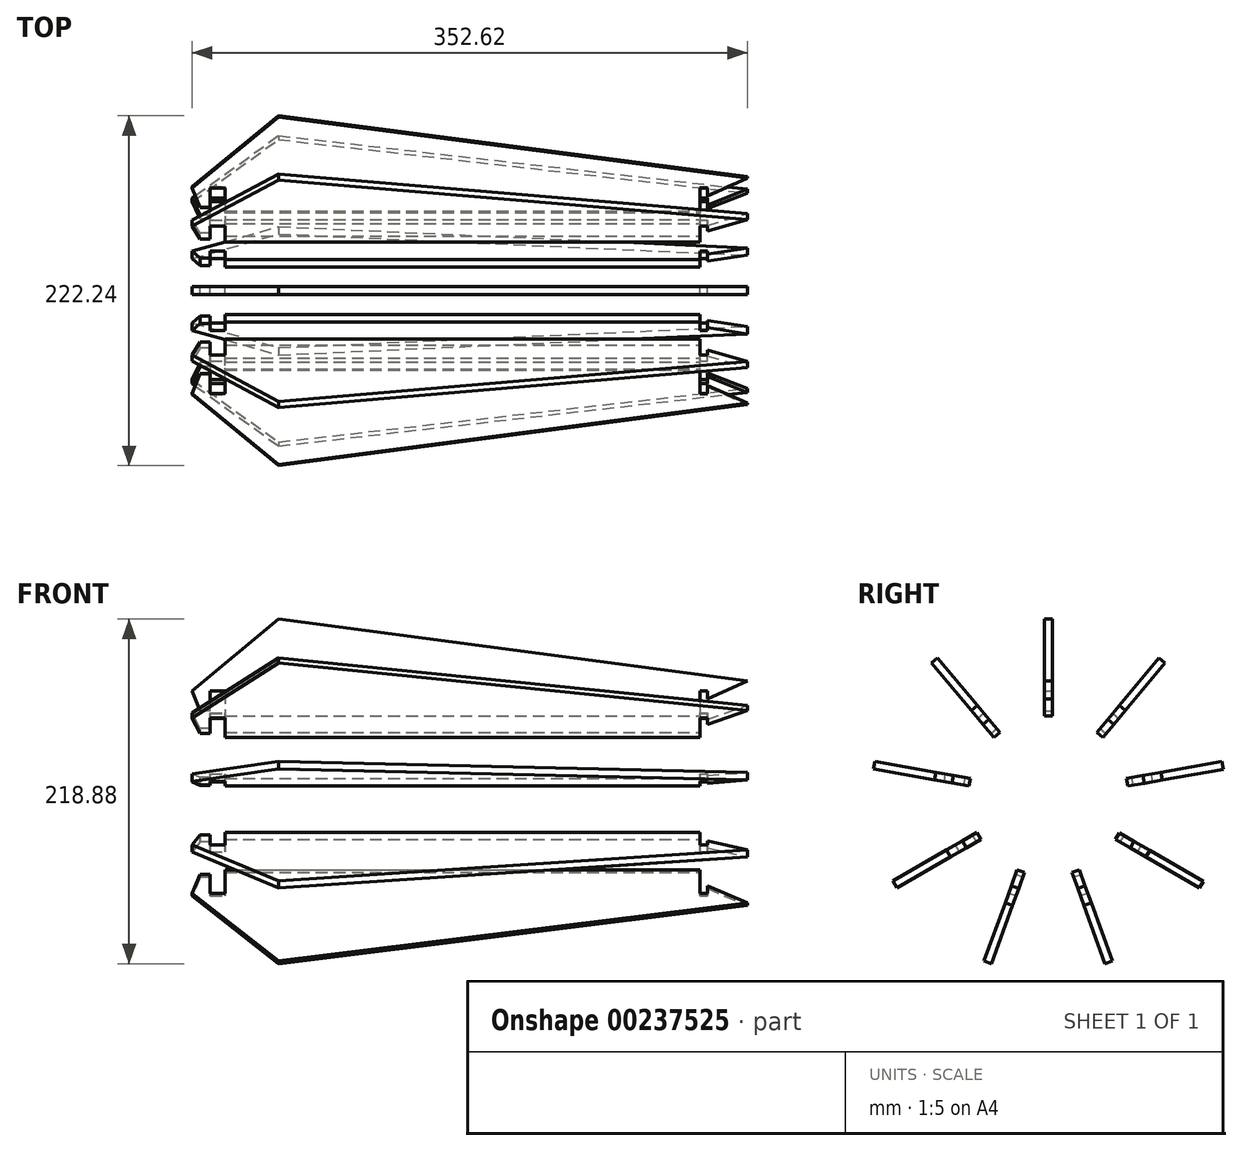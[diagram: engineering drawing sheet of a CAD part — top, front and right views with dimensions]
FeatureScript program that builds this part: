
annotation { "Feature Type Name" : "Feature", "Feature Type Description" : "" }
export const myFeature = defineFeature(function(context is Context, id is Id, definition is map)
    precondition{}
    {
        {
            var Q0;
            Q0=qCreatedBy(makeId("Front.planeOp"),FACE);
            var sketch = newSketch(context, id + "F0", { "sketchPlane" : qUnion([Q0])});
            skLineSegment(sketch, "E0", {"start": v(0, 0) * mm, "end": v(0, 12.7) * mm});
            skLineSegment(sketch, "E1", {"start": v(0, 12.7) * mm, "end": v(9.46, 12.7) * mm});
            skLineSegment(sketch, "E2", {"start": v(0, 0) * mm, "end": v(-6.35, 0) * mm});
            skLineSegment(sketch, "E3", {"start": v(-6.35, 0) * mm, "end": v(-11.43, 12.7) * mm});
            skLineSegment(sketch, "E4", {"start": v(-11.43, 12.7) * mm, "end": v(0, 22.23) * mm});
            skLineSegment(sketch, "E5", {"start": v(0, 22.23) * mm, "end": v(43.43, 58.42) * mm});
            skLineSegment(sketch, "E6", {"start": v(310.96, 12.7) * mm, "end": v(310.96, -3.18) * mm});
            skLineSegment(sketch, "E7", {"start": v(9.46, -3.18) * mm, "end": v(310.96, -3.18) * mm});
            skLineSegment(sketch, "E8", {"start": v(310.96, 12.7) * mm, "end": v(315.79, 12.7) * mm});
            skLineSegment(sketch, "E9", {"start": v(315.79, 12.7) * mm, "end": v(315.79, 7.62) * mm});
            skLineSegment(sketch, "E10", {"start": v(315.79, 7.62) * mm, "end": v(341.19, 19.05) * mm});
            skLineSegment(sketch, "E11", {"start": v(43.43, 58.42) * mm, "end": v(341.19, 19.05) * mm});
            skLineSegment(sketch, "E12", {"start": v(9.46, 12.7) * mm, "end": v(310.96, 12.7) * mm, "construction": true});
            skLineSegment(sketch, "E13", {"start": v(9.46, 12.7) * mm, "end": v(9.46, 12.7) * mm});
            skLineSegment(sketch, "E14", {"start": v(9.46, 12.7) * mm, "end": v(9.46, -3.18) * mm});
            skSolve(sketch);
        }
        {
            var Q0;
            Q0=makeQuery(id+"F0.imprint","IMPRINT",FACE,{"disambiguationData":[TD([[makeQuery(id+"F0.imprint","IMPRINT",EDGE,{"derivedFrom":sQuery(id+"F0.wireOp",EDGE,"E0")}),1.0]])]});
            extrude(context, id + "F1", {"entities" : qUnion([Q0]), "depth" : 4.95 * mm});
        }
        {
            var Q0;
            Q0=makeQuery(id+"F1.opExtrude","SWEPT_FACE",FACE,{"disambiguationData":[OSD([sQuery(id+"F0.wireOp",EDGE,"E14")])]});
            var sketch = newSketch(context, id + "F2", { "sketchPlane" : qUnion([Q0])});
            skPoint(sketch, "E15", {"position": v(2.54, -3.18) * mm});
            skCircle(sketch, "E16", {"center": v(2.54, -53.98) * mm, "radius": 50.8 * mm, "construction": true});
            skSolve(sketch);
        }
        {
            var Q0;
            Q0=makeQuery(id+"F1.opExtrude","CAP_FACE",FACE,{"disambiguationData":[OSD([sQuery(id+"F0.wireOp",EDGE,"E0"),sQuery(id+"F0.wireOp",EDGE,"E1"),sQuery(id+"F0.wireOp",EDGE,"E2"),sQuery(id+"F0.wireOp",EDGE,"E3"),sQuery(id+"F0.wireOp",EDGE,"E4"),sQuery(id+"F0.wireOp",EDGE,"E5"),sQuery(id+"F0.wireOp",EDGE,"E6"),sQuery(id+"F0.wireOp",EDGE,"T48b2aqO-5OnB-VpQv-qECW-1JBLnEAKpYdm"),sQuery(id+"F0.wireOp",EDGE,"E7"),sQuery(id+"F0.wireOp",EDGE,"E8"),sQuery(id+"F0.wireOp",EDGE,"E9"),sQuery(id+"F0.wireOp",EDGE,"E10"),sQuery(id+"F0.wireOp",EDGE,"E11")])],"isStart":false});
            var Q1;
            Q1=makeQuery(id+"F1.opExtrude","CAP_FACE",FACE,{"disambiguationData":[OSD([sQuery(id+"F0.wireOp",EDGE,"E0"),sQuery(id+"F0.wireOp",EDGE,"E1"),sQuery(id+"F0.wireOp",EDGE,"E2"),sQuery(id+"F0.wireOp",EDGE,"E3"),sQuery(id+"F0.wireOp",EDGE,"E4"),sQuery(id+"F0.wireOp",EDGE,"E5"),sQuery(id+"F0.wireOp",EDGE,"E6"),sQuery(id+"F0.wireOp",EDGE,"T48b2aqO-5OnB-VpQv-qECW-1JBLnEAKpYdm"),sQuery(id+"F0.wireOp",EDGE,"E7"),sQuery(id+"F0.wireOp",EDGE,"E8"),sQuery(id+"F0.wireOp",EDGE,"E9"),sQuery(id+"F0.wireOp",EDGE,"E10"),sQuery(id+"F0.wireOp",EDGE,"E11")])],"isStart":true});
            cPlane(context, id + "F3", {"entities" : qUnion([Q0, Q1]), "cplaneType" : CPlaneType.MID_PLANE, "offset" : 25.4 * mm, "width" : 152.4 * mm, "height" : 152.4 * mm});
        }
        {
            var Q0;
            Q0=makeQuery(id+"F1.opExtrude","SWEPT_BODY",BODY,{"disambiguationData":[OSD([sQuery(id+"F0.wireOp",EDGE,"E0"),sQuery(id+"F0.wireOp",EDGE,"E1"),sQuery(id+"F0.wireOp",EDGE,"E2"),sQuery(id+"F0.wireOp",EDGE,"E3"),sQuery(id+"F0.wireOp",EDGE,"E4"),sQuery(id+"F0.wireOp",EDGE,"E5"),sQuery(id+"F0.wireOp",EDGE,"E6"),sQuery(id+"F0.wireOp",EDGE,"T48b2aqO-5OnB-VpQv-qECW-1JBLnEAKpYdm"),sQuery(id+"F0.wireOp",EDGE,"E7"),sQuery(id+"F0.wireOp",EDGE,"E8"),sQuery(id+"F0.wireOp",EDGE,"E9"),sQuery(id+"F0.wireOp",EDGE,"E10"),sQuery(id+"F0.wireOp",EDGE,"E11")])]});
            var Q1;
            Q1=sQuery(id+"F2.wireOp",EDGE,"E16");
            circularPattern(context, id + "F4", {"entities" : qUnion([Q0]), "axis" : qUnion([Q1]), "angle" : 360 * degree, "instanceCount" : 9, "equalSpace" : true});
        }
    });
